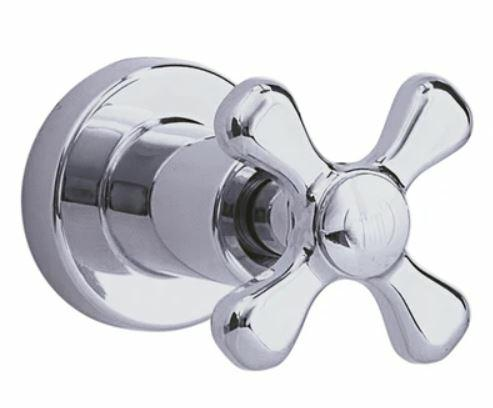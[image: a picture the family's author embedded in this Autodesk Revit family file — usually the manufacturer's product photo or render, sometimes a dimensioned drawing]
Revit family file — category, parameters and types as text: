
# Revit family: 01-0823-11 REGISTRO DUCHA COLECCION CALIMA
name_source: partatom
category: Plumbing Fixtures
revit_build: Autodesk Revit 2018 (Build: 20170223_1515(x64)
units: mm (PartAtom-declared; Revit-internal decimal feet)

## family parameters
Cut with Voids When Loaded = No
Host = Face
OmniClass Number = 23.31.11.00
Part Type = Normal
Room Calculation Point = No
Round Connector Dimension = Use Diameter
Shared = No

## types (1)
- 01-0823-11
    Alto = 85 mm  [stored 0.278871 ft]
    Ancho manija = 72 mm  [stored 0.23622 ft]
    CW Connection = Yes
    Default Elevation = 0 mm  [stored 0 ft]
    Description = Registro
    Dim escudo = 60 mm  [stored 0.19685 ft]
    HW Connection = Yes
    Link Ficha Tecnica = http://infotecnica.gricol.com
    Manufacturer = Gricol
    Metal Zamak Cromado = Metal Zamak Cromado
    Model = 01-0823-11
    Plastico - ABS Cromado = Plastico - ABS Cromado
    Product Name = REGISTRO DUCHA ATLANTICO
    Type Image = <None>
    URL = https://www.gricol.com
    Vent Connection = No
    Waste Connection = No

note: [stored X ft] marks values corroborated as IEEE doubles in the binary element streams (Revit-internal decimal feet)

## geometry (parser evidence)
native form markers: Blend x2, Sweep x8
no freeform markers — native parametric forms only
